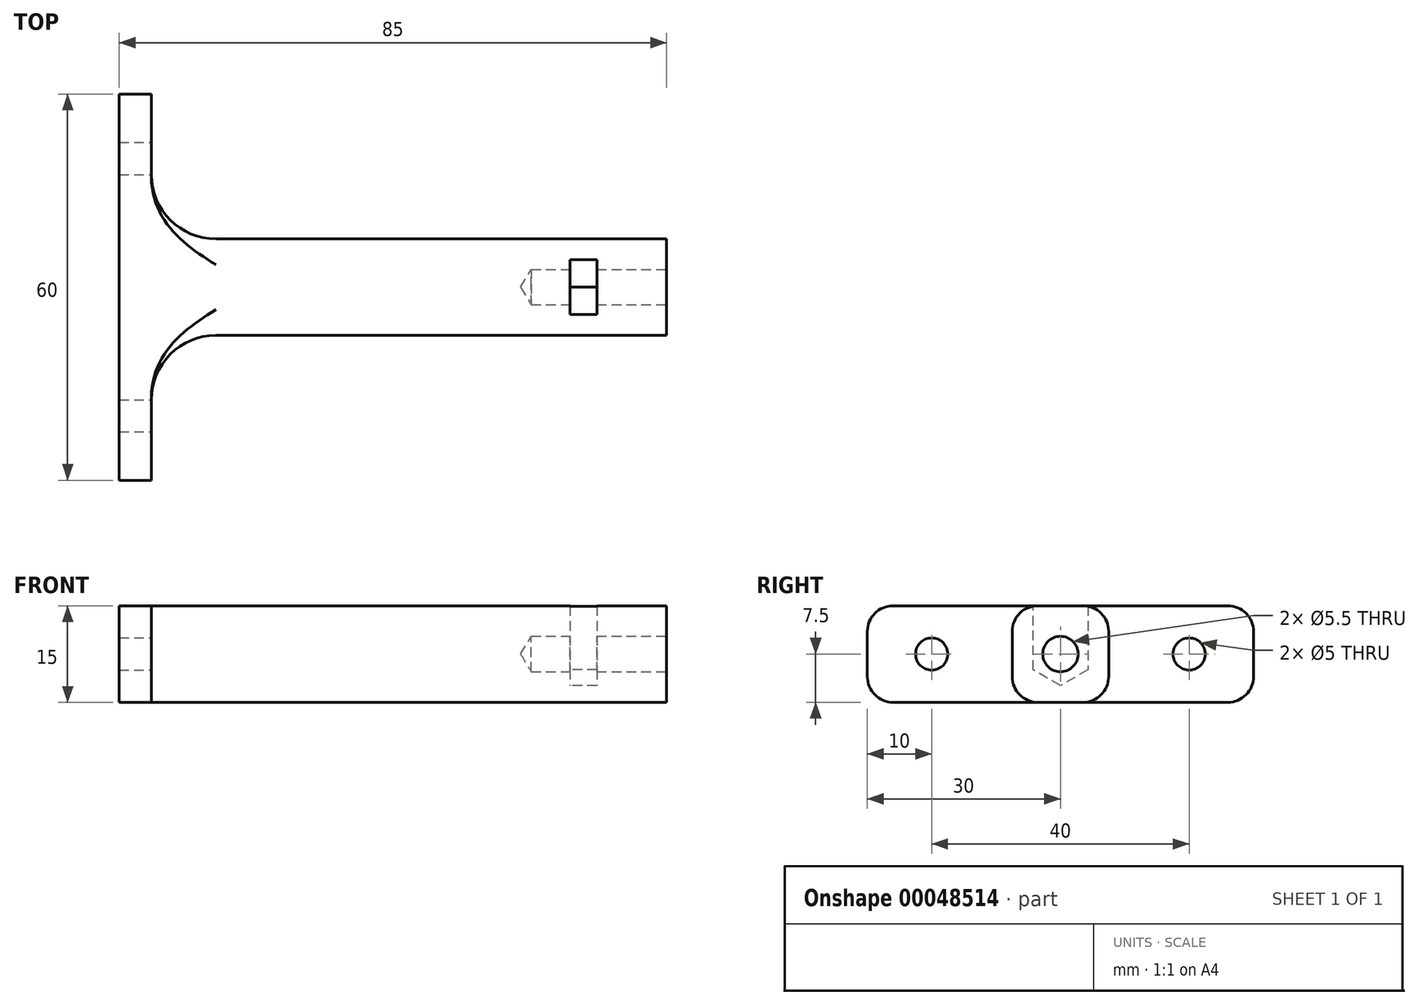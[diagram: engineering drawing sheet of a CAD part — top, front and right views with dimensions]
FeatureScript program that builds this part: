
annotation { "Feature Type Name" : "Feature", "Feature Type Description" : "" }
export const myFeature = defineFeature(function(context is Context, id is Id, definition is map)
    precondition{}
    {
        {
            var Q0;
            Q0=qCreatedBy(makeId("Top.planeOp"),FACE);
            var sketch = newSketch(context, id + "F0", { "sketchPlane" : qUnion([Q0])});
            skLineSegment(sketch, "E0.bottom", {"start": v(-22.39, 30) * mm, "end": v(-17.39, 30) * mm});
            skLineSegment(sketch, "E0.top", {"start": v(-22.39, -30) * mm, "end": v(-17.39, -30) * mm});
            skLineSegment(sketch, "E0.left", {"start": v(-22.39, 30) * mm, "end": v(-22.39, -30) * mm});
            skLineSegment(sketch, "E0.right", {"start": v(-17.39, 30) * mm, "end": v(-17.39, 7.5) * mm});
            skLineSegment(sketch, "E1.rect.bottom", {"start": v(-17.39, 7.5) * mm, "end": v(62.61, 7.5) * mm});
            skLineSegment(sketch, "E1.rect.top", {"start": v(-17.39, -7.5) * mm, "end": v(62.61, -7.5) * mm});
            skLineSegment(sketch, "E1.rect.right", {"start": v(62.61, 7.5) * mm, "end": v(62.61, -7.5) * mm});
            skPoint(sketch, "E1.rect.middle", {"position": v(22.61, 0) * mm});
            skLineSegment(sketch, "E2.trimOffspring", {"start": v(-17.39, -7.5) * mm, "end": v(-17.39, -30) * mm});
            skPoint(sketch, "E3.orphan", {"position": v(-22.39, 0) * mm});
            skPoint(sketch, "E4.end.orphan", {"position": v(67.61, 0) * mm});
            skSolve(sketch);
        }
        {
            var Q0;
            Q0=makeQuery(id+"F0.imprint","IMPRINT",FACE,{"disambiguationData":[TD([[makeQuery(id+"F0.imprint","IMPRINT",EDGE,{"derivedFrom":sQuery(id+"F0.wireOp",EDGE,"E0.bottom")}),-1.0]])]});
            extrude(context, id + "F1", {"entities" : qUnion([Q0]), "depth" : 15 * mm});
        }
        {
            var Q0;
            Q0=makeQuery(id+"F1.opExtrude","SWEPT_FACE",FACE,{"disambiguationData":[OSD([sQuery(id+"F0.wireOp",EDGE,"E1.rect.right")])]});
            var sketch = newSketch(context, id + "F2", { "sketchPlane" : qUnion([Q0])});
            skLineSegment(sketch, "E5", {"start": v(7.5, 15) * mm, "end": v(-7.5, 0) * mm, "construction": true});
            skLineSegment(sketch, "E6", {"start": v(-7.5, 15) * mm, "end": v(7.5, 0) * mm, "construction": true});
            skPoint(sketch, "E7", {"position": v(0, 7.5) * mm});
            skSolve(sketch);
        }
        {
            var Q0;
            Q0=sQuery(id+"F2.wireOp",VERTEX,"E7");
            var Q1;
            Q1=makeQuery(id+"F1.opExtrude","SWEPT_BODY",BODY,{"disambiguationData":[OSD([sQuery(id+"F0.wireOp",EDGE,"E0.bottom"),sQuery(id+"F0.wireOp",EDGE,"E0.top"),sQuery(id+"F0.wireOp",EDGE,"E0.left"),sQuery(id+"F0.wireOp",EDGE,"E0.right"),sQuery(id+"F0.wireOp",EDGE,"E1.rect.bottom"),sQuery(id+"F0.wireOp",EDGE,"E1.rect.top"),sQuery(id+"F0.wireOp",EDGE,"E1.rect.right"),sQuery(id+"F0.wireOp",EDGE,"E2.trimOffspring")])]});
            hole(context, id + "F3", {"style" : HoleStyle.SIMPLE, "holeDiameter" : 5.5 * mm, "endStyle" : HoleEndStyle.BLIND, "holeDepth" : 21 * mm, "locations" : qUnion([Q0]), "scope" : qUnion([Q1])});
        }
        {
            var Q0;
            Q0=makeQuery(id+"F1.opExtrude","SWEPT_FACE",FACE,{"disambiguationData":[OSD([sQuery(id+"F0.wireOp",EDGE,"E2.trimOffspring")])]});
            var sketch = newSketch(context, id + "F4", { "sketchPlane" : qUnion([Q0])});
            skLineSegment(sketch, "E8", {"start": v(-30, 7.5) * mm, "end": v(54.69, 7.5) * mm, "construction": true});
            skPoint(sketch, "E9", {"position": v(-20, 7.5) * mm});
            skPoint(sketch, "E10", {"position": v(20, 7.5) * mm});
            skSolve(sketch);
        }
        {
            var Q0;
            Q0=sQuery(id+"F4.wireOp",VERTEX,"E9");
            var Q1;
            Q1=sQuery(id+"F4.wireOp",VERTEX,"E10");
            var Q2;
            Q2=makeQuery(id+"F1.opExtrude","SWEPT_BODY",BODY,{"disambiguationData":[OSD([sQuery(id+"F0.wireOp",EDGE,"E0.bottom"),sQuery(id+"F0.wireOp",EDGE,"E0.top"),sQuery(id+"F0.wireOp",EDGE,"E0.left"),sQuery(id+"F0.wireOp",EDGE,"E0.right"),sQuery(id+"F0.wireOp",EDGE,"E1.rect.bottom"),sQuery(id+"F0.wireOp",EDGE,"E1.rect.top"),sQuery(id+"F0.wireOp",EDGE,"E1.rect.right"),sQuery(id+"F0.wireOp",EDGE,"E2.trimOffspring")])]});
            hole(context, id + "F5", {"style" : HoleStyle.SIMPLE, "holeDiameter" : 5 * mm, "endStyle" : HoleEndStyle.THROUGH, "locations" : qUnion([Q0, Q1]), "scope" : qUnion([Q2])});
        }
        {
            var Q0;
            Q0=makeQuery(id+"F1.opExtrude","CAP_EDGE",EDGE,{"disambiguationData":[OSD([sQuery(id+"F0.wireOp",EDGE,"E1.rect.top")])],"isStart":false});
            var Q1;
            Q1=makeQuery(id+"F1.opExtrude","CAP_EDGE",EDGE,{"disambiguationData":[OSD([sQuery(id+"F0.wireOp",EDGE,"E1.rect.bottom")])],"isStart":false});
            var Q2;
            Q2=makeQuery(id+"F1.opExtrude","CAP_EDGE",EDGE,{"disambiguationData":[OSD([sQuery(id+"F0.wireOp",EDGE,"E1.rect.top")])],"isStart":true});
            var Q3;
            Q3=makeQuery(id+"F1.opExtrude","CAP_EDGE",EDGE,{"disambiguationData":[OSD([sQuery(id+"F0.wireOp",EDGE,"E1.rect.bottom")])],"isStart":true});
            var Q4;
            Q4=makeQuery(id+"F1.opExtrude","CAP_EDGE",EDGE,{"disambiguationData":[OSD([sQuery(id+"F0.wireOp",EDGE,"E0.top")])],"isStart":false});
            var Q5;
            Q5=makeQuery(id+"F1.opExtrude","CAP_EDGE",EDGE,{"disambiguationData":[OSD([sQuery(id+"F0.wireOp",EDGE,"E0.top")])],"isStart":true});
            var Q6;
            Q6=makeQuery(id+"F1.opExtrude","CAP_EDGE",EDGE,{"disambiguationData":[OSD([sQuery(id+"F0.wireOp",EDGE,"E0.bottom")])],"isStart":false});
            var Q7;
            Q7=makeQuery(id+"F1.opExtrude","CAP_EDGE",EDGE,{"disambiguationData":[OSD([sQuery(id+"F0.wireOp",EDGE,"E0.bottom")])],"isStart":true});
            fillet(context, id + "F6", {"entities" : qUnion([Q0, Q1, Q2, Q3, Q4, Q5, Q6, Q7]), "radius" : 4 * mm, "tangentPropagation" : true, "allowEdgeOverflow" : false});
        }
        {
            var Q0;
            Q0=makeQuery(id+"F1.opExtrude","SWEPT_EDGE",EDGE,{"disambiguationData":[OSD([sQuery(id+"F0.wireOp",EDGE,"E1.rect.top"),sQuery(id+"F0.wireOp",EDGE,"E2.trimOffspring")])]});
            var Q1;
            Q1=makeQuery(id+"F1.opExtrude","SWEPT_EDGE",EDGE,{"disambiguationData":[OSD([sQuery(id+"F0.wireOp",EDGE,"E0.right"),sQuery(id+"F0.wireOp",EDGE,"E1.rect.bottom")])]});
            fillet(context, id + "F7", {"entities" : qUnion([Q0, Q1]), "radius" : 10 * mm, "tangentPropagation" : true, "allowEdgeOverflow" : false});
        }
        {
            var Q0;
            Q0=makeQuery(id+"F1.opExtrude","SWEPT_FACE",FACE,{"disambiguationData":[OSD([sQuery(id+"F0.wireOp",EDGE,"E1.rect.right")])]});
            cPlane(context, id + "F8", {"entities" : qUnion([Q0]), "cplaneType" : CPlaneType.OFFSET, "offset" : 15 * mm, "oppositeDirection" : true, "width" : 150 * mm, "height" : 150 * mm});
        }
        {
            var Q0;
            Q0=qCreatedBy(id+"F8.planeOp",FACE);
            var sketch = newSketch(context, id + "F9", { "sketchPlane" : qUnion([Q0])});
            skCircle(sketch, "E11.0", {"center": v(0, 7.5) * mm, "radius": 2.75 * mm, "construction": true});
            skCircle(sketch, "E12.cCircle", {"center": v(0, 7.5) * mm, "radius": 4.9 * mm, "construction": true});
            skLineSegment(sketch, "E12.0", {"start": v(4.25, 5.05) * mm, "end": v(0, 2.6) * mm});
            skLineSegment(sketch, "E12.1", {"start": v(0, 2.6) * mm, "end": v(-4.25, 5.05) * mm});
            skLineSegment(sketch, "E12.2", {"start": v(-4.25, 5.05) * mm, "end": v(-4.25, 9.95) * mm});
            skLineSegment(sketch, "E12.5", {"start": v(4.25, 9.95) * mm, "end": v(4.25, 5.05) * mm});
            skLineSegment(sketch, "E13", {"start": v(-4.25, 9.95) * mm, "end": v(-4.25, 17.46) * mm});
            skLineSegment(sketch, "E14", {"start": v(-4.25, 17.46) * mm, "end": v(4.25, 17.46) * mm});
            skLineSegment(sketch, "E15", {"start": v(4.25, 17.46) * mm, "end": v(4.25, 9.95) * mm});
            skSolve(sketch);
        }
        {
            var Q0;
            Q0 = qSketchRegion(id + "F9", true);
            extrude(context, id + "F10", {"entities" : qUnion([Q0]), "operationType" : NewBodyOperationType.REMOVE, "depth" : 4.2 * mm});
        }
    });
